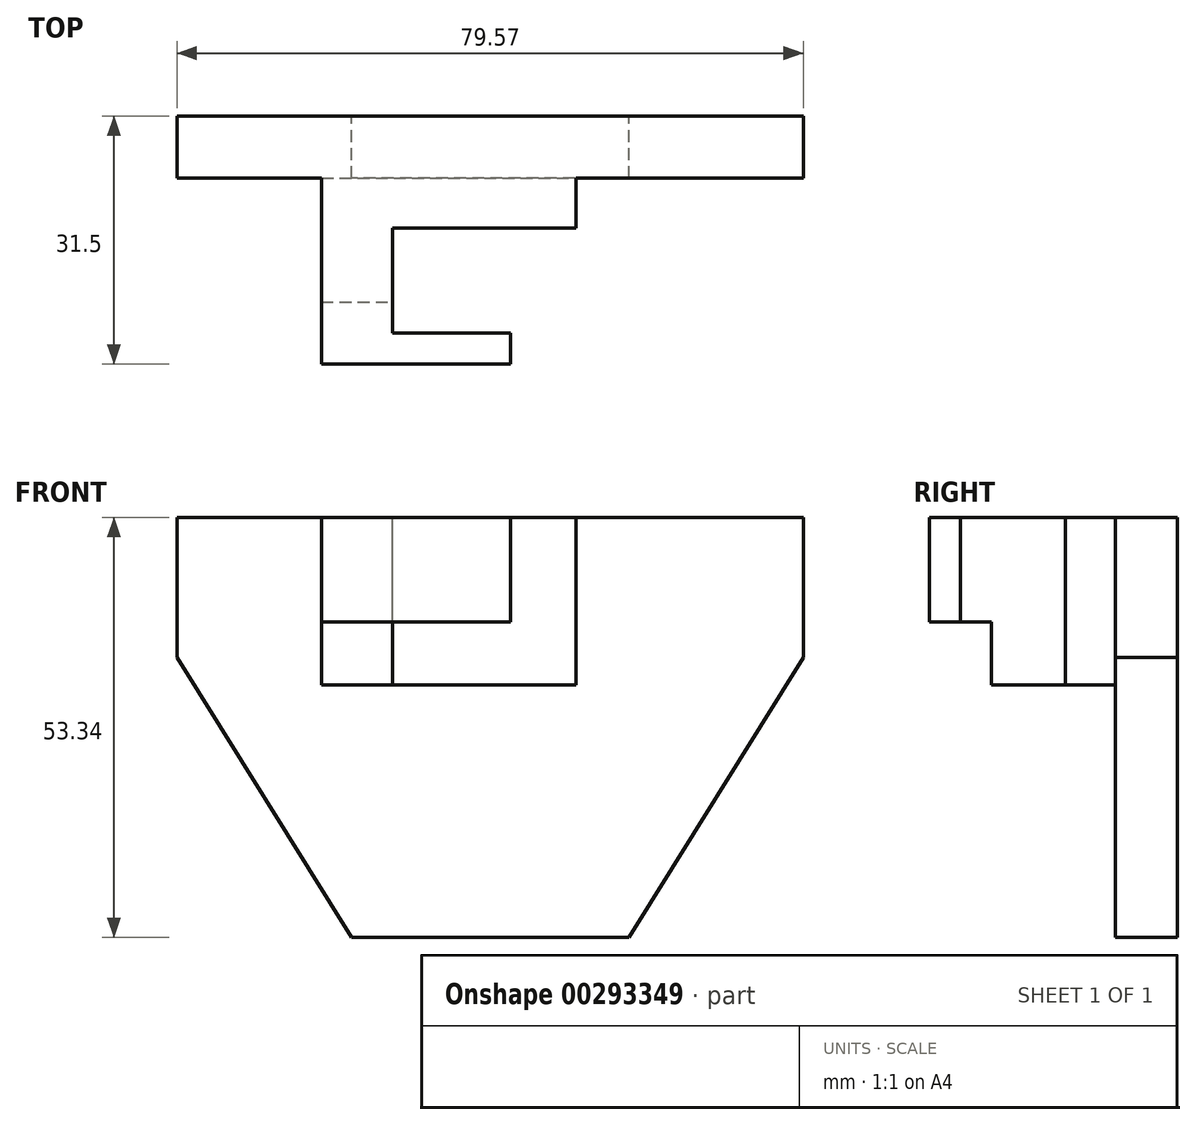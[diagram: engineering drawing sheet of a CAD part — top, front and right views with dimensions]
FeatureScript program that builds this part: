
annotation { "Feature Type Name" : "Feature", "Feature Type Description" : "" }
export const myFeature = defineFeature(function(context is Context, id is Id, definition is map)
    precondition{}
    {
        {
            var Q0;
            Q0=qCreatedBy(makeId("Front.planeOp"),FACE);
            var sketch = newSketch(context, id + "F0", { "sketchPlane" : qUnion([Q0])});
            skLineSegment(sketch, "E0", {"start": v(-43.43, 39.2) * mm, "end": v(36.14, 39.2) * mm});
            skLineSegment(sketch, "E1", {"start": v(36.14, 39.2) * mm, "end": v(36.14, 21.42) * mm});
            skLineSegment(sketch, "E2", {"start": v(36.14, 21.42) * mm, "end": v(36.14, 39.2) * mm});
            skLineSegment(sketch, "E3", {"start": v(-43.43, 39.2) * mm, "end": v(-43.43, 21.42) * mm});
            skLineSegment(sketch, "E4", {"start": v(-43.43, 21.42) * mm, "end": v(-21.28, -14.14) * mm});
            skLineSegment(sketch, "E5", {"start": v(36.14, 21.42) * mm, "end": v(14, -14.14) * mm});
            skLineSegment(sketch, "E6", {"start": v(14, -14.14) * mm, "end": v(-21.28, -14.14) * mm});
            skSolve(sketch);
        }
        {
            var Q0;
            Q0 = qSketchRegion(id + "F0", true);
            extrude(context, id + "F1", {"entities" : qUnion([Q0]), "depth" : 7.87 * mm});
        }
        {
            var Q0;
            Q0=makeQuery(id+"F1.opExtrude","CAP_FACE",FACE,{"disambiguationData":[OSD([sQuery(id+"F0.wireOp",EDGE,"E0"),sQuery(id+"F0.wireOp",EDGE,"E2"),sQuery(id+"F0.wireOp",EDGE,"E3"),sQuery(id+"F0.wireOp",EDGE,"E4"),sQuery(id+"F0.wireOp",EDGE,"E5"),sQuery(id+"F0.wireOp",EDGE,"E6")])],"isStart":false});
            var sketch = newSketch(context, id + "F2", { "sketchPlane" : qUnion([Q0])});
            skLineSegment(sketch, "E7", {"start": v(-25.07, 39.2) * mm, "end": v(-25.07, 17.93) * mm});
            skLineSegment(sketch, "E8", {"start": v(-25.07, 17.93) * mm, "end": v(7.29, 17.93) * mm});
            skLineSegment(sketch, "E9", {"start": v(7.29, 17.93) * mm, "end": v(7.29, 39.2) * mm});
            skLineSegment(sketch, "E10", {"start": v(7.29, 39.2) * mm, "end": v(-25.07, 39.2) * mm});
            skLineSegment(sketch, "E11", {"start": v(-16.32, 17.93) * mm, "end": v(-16.32, 39.2) * mm});
            skSolve(sketch);
        }
        {
            var Q0;
            Q0 = qSketchRegion(id + "F2", true);
            extrude(context, id + "F3", {"entities" : qUnion([Q0]), "operationType" : NewBodyOperationType.ADD, "depth" : 6.35 * mm});
        }
        {
            var Q0;
            Q0=makeQuery(id+"F3.opExtrude","CAP_FACE",FACE,{"disambiguationData":[OSD([sQuery(id+"F2.wireOp",EDGE,"E7"),sQuery(id+"F2.wireOp",EDGE,"E8"),sQuery(id+"F2.wireOp",EDGE,"E9"),sQuery(id+"F2.wireOp",EDGE,"E10")])],"isStart":false});
            var sketch = newSketch(context, id + "F4", { "sketchPlane" : qUnion([Q0])});
            skLineSegment(sketch, "E12", {"start": v(-16.03, 17.93) * mm, "end": v(-16.03, 39.2) * mm});
            skSolve(sketch);
        }
        {
            var Q0;
            Q0 = qSketchRegion(id + "F4", true);
            var Q1;
            {var subQ0=sQuery(id+"F4.wireOp",EDGE,"E12");Q1=makeQuery(id+"F4.imprint","IMPRINT",FACE,{"disambiguationData":[TD([[makeQuery(id+"F4.imprint","IMPRINT",EDGE,{"derivedFrom":subQ0}),1.0]])]});}
            extrude(context, id + "F5", {"entities" : qUnion([Q0, Q1]), "operationType" : NewBodyOperationType.ADD, "depth" : 17.27 * mm});
        }
        {
            var Q0;
            Q0=makeQuery(id+"F5.opExtrude","CAP_FACE",FACE,{"disambiguationData":[OSD([sQuery(id+"F2.wireOp",EDGE,"E7"),sQuery(id+"F2.wireOp",EDGE,"E8"),sQuery(id+"F2.wireOp",EDGE,"E10"),sQuery(id+"F4.wireOp",EDGE,"E12")])],"isStart":false});
            var sketch = newSketch(context, id + "F6", { "sketchPlane" : qUnion([Q0])});
            skLineSegment(sketch, "E13", {"start": v(-16.03, 25.94) * mm, "end": v(-25.07, 25.94) * mm});
            skSolve(sketch);
        }
        {
            var Q0;
            Q0 = qSketchRegion(id + "F6", true);
            var Q1;
            {var subQ0=sQuery(id+"F6.wireOp",EDGE,"E13");Q1=makeQuery(id+"F6.imprint","IMPRINT",FACE,{"disambiguationData":[TD([[makeQuery(id+"F6.imprint","IMPRINT",EDGE,{"derivedFrom":subQ0}),1.0]])]});}
            extrude(context, id + "F7", {"entities" : qUnion([Q0, Q1]), "operationType" : NewBodyOperationType.REMOVE, "oppositeDirection" : true, "depth" : 7.87 * mm});
        }
        {
            var Q0;
            Q0=makeQuery(id+"F5.opExtrude","SWEPT_FACE",FACE,{"disambiguationData":[OSD([sQuery(id+"F4.wireOp",EDGE,"E12")])]});
            var sketch = newSketch(context, id + "F8", { "sketchPlane" : qUnion([Q0])});
            skLineSegment(sketch, "E14", {"start": v(-27.56, 25.94) * mm, "end": v(-27.56, 39.2) * mm});
            skSolve(sketch);
        }
        {
            var Q0;
            Q0 = qSketchRegion(id + "F8", true);
            var Q1;
            {var subQ0=sQuery(id+"F8.wireOp",EDGE,"E14");Q1=makeQuery(id+"F8.imprint","IMPRINT",FACE,{"disambiguationData":[TD([[makeQuery(id+"F8.imprint","IMPRINT",EDGE,{"derivedFrom":subQ0}),1.0]])]});}
            extrude(context, id + "F9", {"entities" : qUnion([Q0, Q1]), "operationType" : NewBodyOperationType.ADD, "depth" : 15 * mm});
        }
    });
